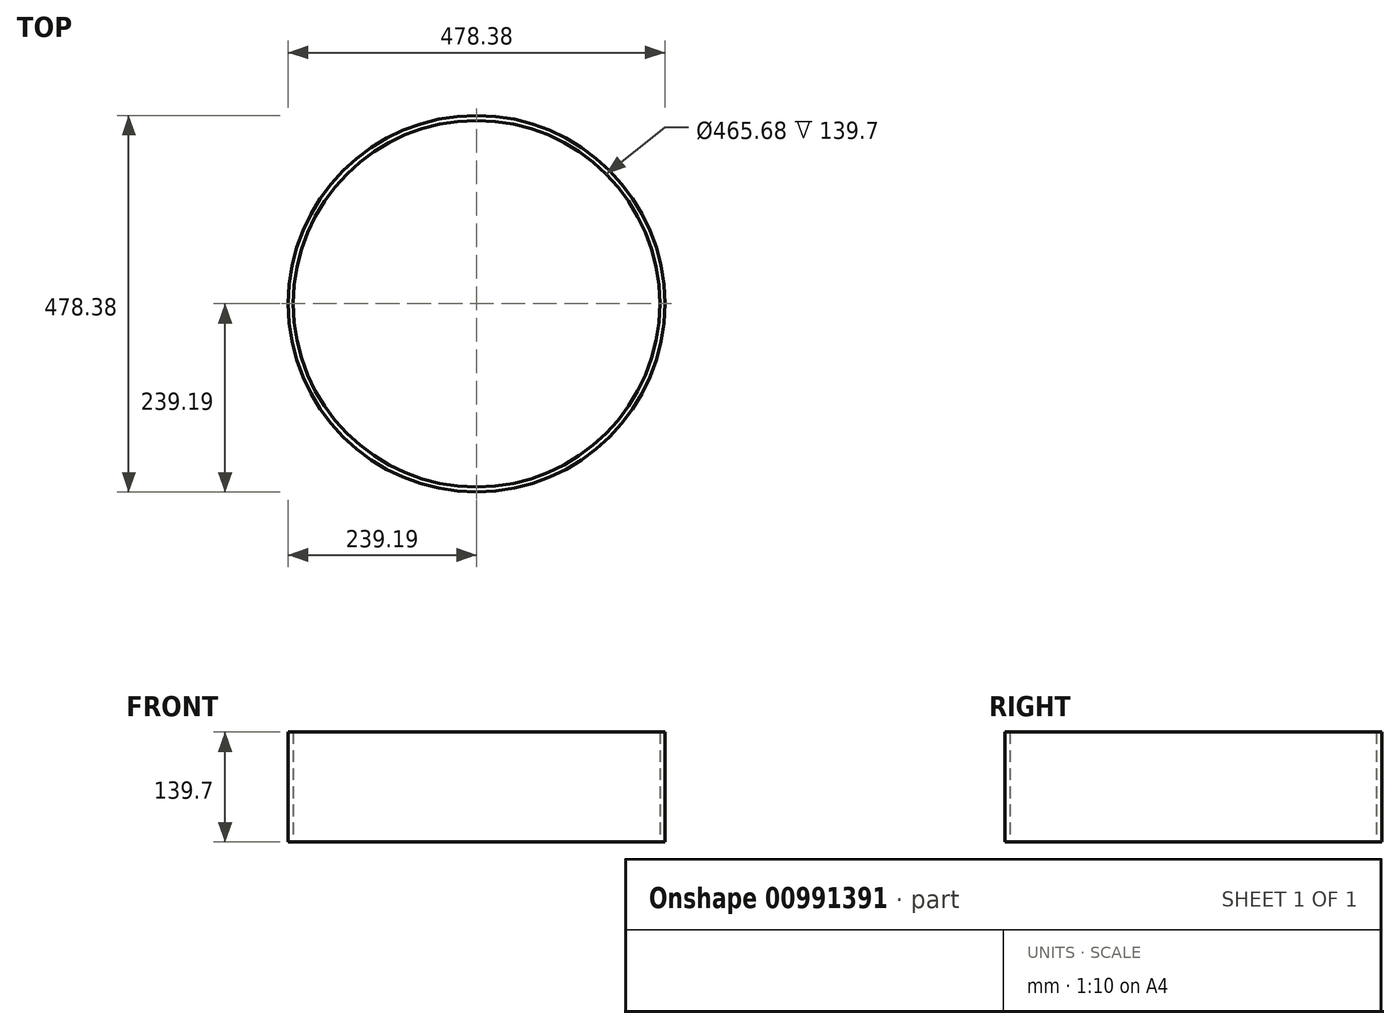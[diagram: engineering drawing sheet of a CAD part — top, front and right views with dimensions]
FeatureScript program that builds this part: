
annotation { "Feature Type Name" : "Feature", "Feature Type Description" : "" }
export const myFeature = defineFeature(function(context is Context, id is Id, definition is map)
    precondition{}
    {
        {
            var Q0;
            Q0=qCreatedBy(makeId("Top.planeOp"),FACE);
            var sketch = newSketch(context, id + "F0", { "sketchPlane" : qUnion([Q0])});
            skCircle(sketch, "E0", {"center": v(0, 0) * mm, "radius": 239.2 * mm});
            skCircle(sketch, "E1.0", {"center": v(0, 0) * mm, "radius": 232.84 * mm});
            skSolve(sketch);
        }
        {
            var Q0;
            Q0=qSketchRegion(id+"F0",true);
            extrude(context, id + "F1", {"entities" : qUnion([Q0]), "endBound" : BoundingType.SYMMETRIC, "depth" : 139.7 * mm, "offsetDistance" : 25.4 * mm});
        }
    });
